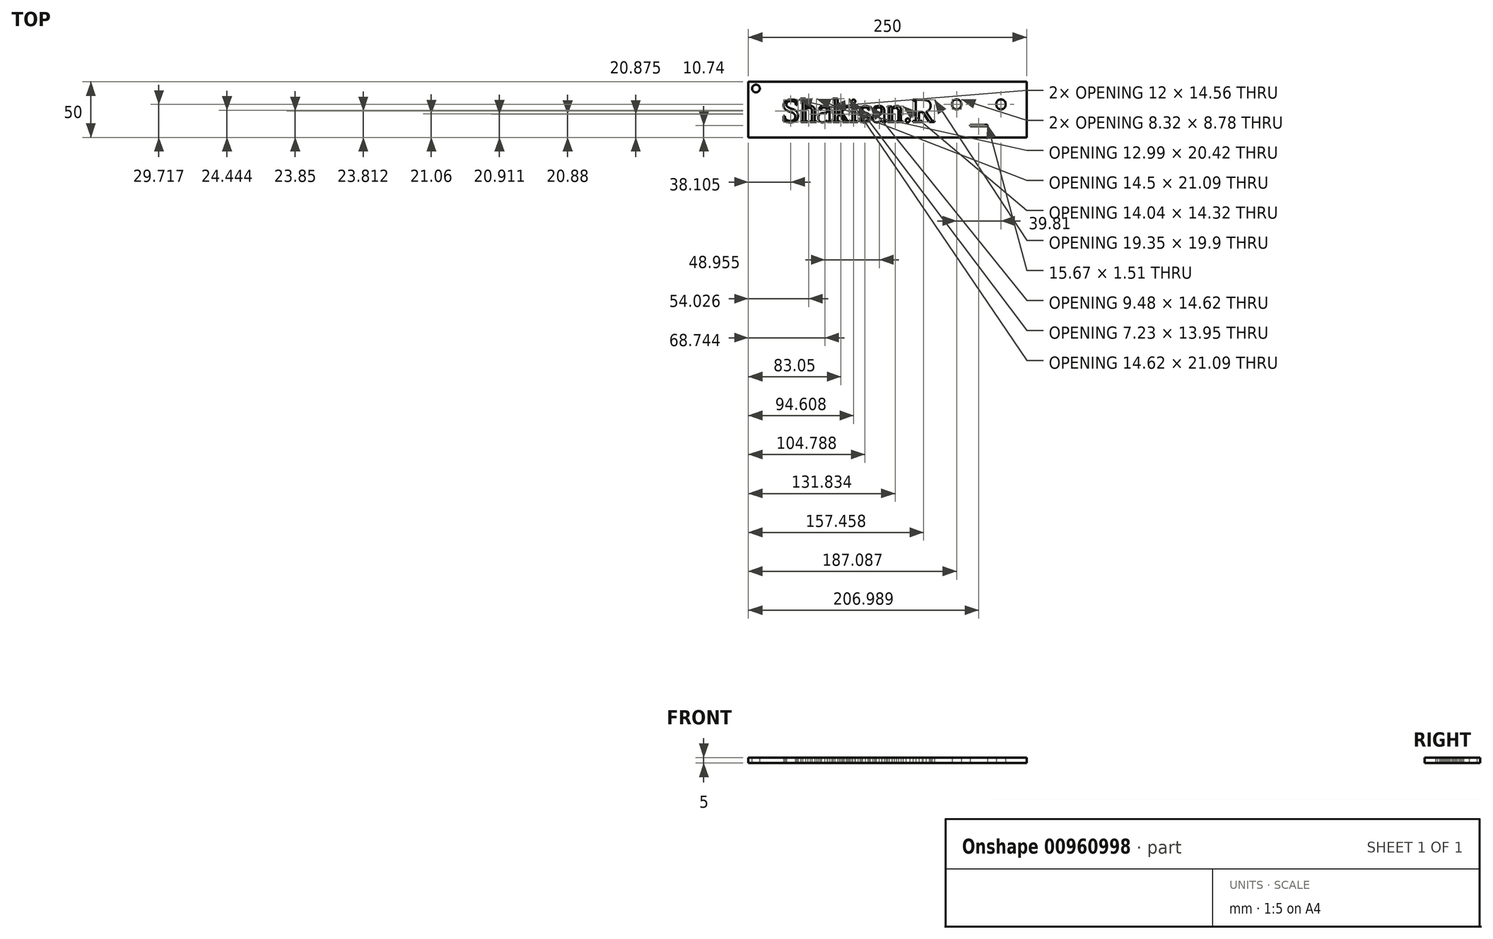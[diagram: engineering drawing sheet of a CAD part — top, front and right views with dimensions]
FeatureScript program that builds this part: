
annotation { "Feature Type Name" : "Feature", "Feature Type Description" : "" }
export const myFeature = defineFeature(function(context is Context, id is Id, definition is map)
    precondition{}
    {
        {
            var Q0;
            Q0=qCreatedBy(makeId("Top.planeOp"),FACE);
            var sketch = newSketch(context, id + "F0", { "sketchPlane" : qUnion([Q0])});
            skLineSegment(sketch, "E0.bottom", {"start": v(21.25, 46.83) * mm, "end": v(271.25, 46.83) * mm});
            skLineSegment(sketch, "E0.top", {"start": v(21.25, -3.17) * mm, "end": v(271.25, -3.17) * mm});
            skLineSegment(sketch, "E0.left", {"start": v(21.25, 46.83) * mm, "end": v(21.25, -3.17) * mm});
            skLineSegment(sketch, "E0.right", {"start": v(271.25, 46.83) * mm, "end": v(271.25, -3.17) * mm});
            skText(sketch, "E1", { "text": "Shakisan.R  º _ º ", "fontName": "Tinos-Regular.ttf"});
            const initialGuessF0  = {"E1": [0.05083, 0.01073, 1, 0, 0.02188]};
            skSetInitialGuess(sketch, initialGuessF0);
            skSolve(sketch);
        }
        {
            var Q0;
            Q0 = qSketchRegion(id + "F0", true);
            extrude(context, id + "F1", {"entities" : qUnion([Q0]), "depth" : 5 * mm, "offsetDistance" : 25 * mm});
        }
        {
            var Q0;
            Q0=makeQuery(id+"F1.opExtrude","CAP_FACE",FACE,{"disambiguationData":[OSD([sQuery(id+"F0.wireOp",EDGE,"E0.bottom"),sQuery(id+"F0.wireOp",EDGE,"E0.top"),sQuery(id+"F0.wireOp",EDGE,"E0.left"),sQuery(id+"F0.wireOp",EDGE,"E0.right"),sQuery(id+"F0.wireOp",EDGE,"52a1acff-9716-4e03-b524-4271869a984e.sketch_text.stroke-0"),sQuery(id+"F0.wireOp",EDGE,"52a1acff-9716-4e03-b524-4271869a984e.sketch_text.stroke-1"),sQuery(id+"F0.wireOp",EDGE,"52a1acff-9716-4e03-b524-4271869a984e.sketch_text.stroke-2"),sQuery(id+"F0.wireOp",EDGE,"52a1acff-9716-4e03-b524-4271869a984e.sketch_text.stroke-3"),sQuery(id+"F0.wireOp",EDGE,"52a1acff-9716-4e03-b524-4271869a984e.sketch_text.stroke-4"),sQuery(id+"F0.wireOp",EDGE,"52a1acff-9716-4e03-b524-4271869a984e.sketch_text.stroke-5"),sQuery(id+"F0.wireOp",EDGE,"52a1acff-9716-4e03-b524-4271869a984e.sketch_text.stroke-6"),sQuery(id+"F0.wireOp",EDGE,"52a1acff-9716-4e03-b524-4271869a984e.sketch_text.stroke-7"),sQuery(id+"F0.wireOp",EDGE,"52a1acff-9716-4e03-b524-4271869a984e.sketch_text.stroke-8"),sQuery(id+"F0.wireOp",EDGE,"52a1acff-9716-4e03-b524-4271869a984e.sketch_text.stroke-9"),sQuery(id+"F0.wireOp",EDGE,"52a1acff-9716-4e03-b524-4271869a984e.sketch_text.stroke-10"),sQuery(id+"F0.wireOp",EDGE,"52a1acff-9716-4e03-b524-4271869a984e.sketch_text.stroke-11"),sQuery(id+"F0.wireOp",EDGE,"52a1acff-9716-4e03-b524-4271869a984e.sketch_text.stroke-12"),sQuery(id+"F0.wireOp",EDGE,"52a1acff-9716-4e03-b524-4271869a984e.sketch_text.stroke-13"),sQuery(id+"F0.wireOp",EDGE,"52a1acff-9716-4e03-b524-4271869a984e.sketch_text.stroke-14"),sQuery(id+"F0.wireOp",EDGE,"52a1acff-9716-4e03-b524-4271869a984e.sketch_text.stroke-15"),sQuery(id+"F0.wireOp",EDGE,"52a1acff-9716-4e03-b524-4271869a984e.sketch_text.stroke-16"),sQuery(id+"F0.wireOp",EDGE,"52a1acff-9716-4e03-b524-4271869a984e.sketch_text.stroke-17"),sQuery(id+"F0.wireOp",EDGE,"52a1acff-9716-4e03-b524-4271869a984e.sketch_text.stroke-18"),sQuery(id+"F0.wireOp",EDGE,"52a1acff-9716-4e03-b524-4271869a984e.sketch_text.stroke-19"),sQuery(id+"F0.wireOp",EDGE,"52a1acff-9716-4e03-b524-4271869a984e.sketch_text.stroke-20"),sQuery(id+"F0.wireOp",EDGE,"52a1acff-9716-4e03-b524-4271869a984e.sketch_text.stroke-21"),sQuery(id+"F0.wireOp",EDGE,"52a1acff-9716-4e03-b524-4271869a984e.sketch_text.stroke-22"),sQuery(id+"F0.wireOp",EDGE,"52a1acff-9716-4e03-b524-4271869a984e.sketch_text.stroke-23"),sQuery(id+"F0.wireOp",EDGE,"52a1acff-9716-4e03-b524-4271869a984e.sketch_text.stroke-24"),sQuery(id+"F0.wireOp",EDGE,"52a1acff-9716-4e03-b524-4271869a984e.sketch_text.stroke-25"),sQuery(id+"F0.wireOp",EDGE,"52a1acff-9716-4e03-b524-4271869a984e.sketch_text.stroke-26"),sQuery(id+"F0.wireOp",EDGE,"52a1acff-9716-4e03-b524-4271869a984e.sketch_text.stroke-27"),sQuery(id+"F0.wireOp",EDGE,"52a1acff-9716-4e03-b524-4271869a984e.sketch_text.stroke-28"),sQuery(id+"F0.wireOp",EDGE,"52a1acff-9716-4e03-b524-4271869a984e.sketch_text.stroke-29"),sQuery(id+"F0.wireOp",EDGE,"52a1acff-9716-4e03-b524-4271869a984e.sketch_text.stroke-30"),sQuery(id+"F0.wireOp",EDGE,"52a1acff-9716-4e03-b524-4271869a984e.sketch_text.stroke-31"),sQuery(id+"F0.wireOp",EDGE,"52a1acff-9716-4e03-b524-4271869a984e.sketch_text.stroke-32"),sQuery(id+"F0.wireOp",EDGE,"52a1acff-9716-4e03-b524-4271869a984e.sketch_text.stroke-33"),sQuery(id+"F0.wireOp",EDGE,"52a1acff-9716-4e03-b524-4271869a984e.sketch_text.stroke-34"),sQuery(id+"F0.wireOp",EDGE,"52a1acff-9716-4e03-b524-4271869a984e.sketch_text.stroke-35"),sQuery(id+"F0.wireOp",EDGE,"52a1acff-9716-4e03-b524-4271869a984e.sketch_text.stroke-36"),sQuery(id+"F0.wireOp",EDGE,"52a1acff-9716-4e03-b524-4271869a984e.sketch_text.stroke-37"),sQuery(id+"F0.wireOp",EDGE,"52a1acff-9716-4e03-b524-4271869a984e.sketch_text.stroke-38"),sQuery(id+"F0.wireOp",EDGE,"52a1acff-9716-4e03-b524-4271869a984e.sketch_text.stroke-39"),sQuery(id+"F0.wireOp",EDGE,"52a1acff-9716-4e03-b524-4271869a984e.sketch_text.stroke-40"),sQuery(id+"F0.wireOp",EDGE,"52a1acff-9716-4e03-b524-4271869a984e.sketch_text.stroke-41"),sQuery(id+"F0.wireOp",EDGE,"52a1acff-9716-4e03-b524-4271869a984e.sketch_text.stroke-42"),sQuery(id+"F0.wireOp",EDGE,"52a1acff-9716-4e03-b524-4271869a984e.sketch_text.stroke-43"),sQuery(id+"F0.wireOp",EDGE,"52a1acff-9716-4e03-b524-4271869a984e.sketch_text.stroke-44"),sQuery(id+"F0.wireOp",EDGE,"52a1acff-9716-4e03-b524-4271869a984e.sketch_text.stroke-45"),sQuery(id+"F0.wireOp",EDGE,"52a1acff-9716-4e03-b524-4271869a984e.sketch_text.stroke-46"),sQuery(id+"F0.wireOp",EDGE,"52a1acff-9716-4e03-b524-4271869a984e.sketch_text.stroke-47"),sQuery(id+"F0.wireOp",EDGE,"52a1acff-9716-4e03-b524-4271869a984e.sketch_text.stroke-48"),sQuery(id+"F0.wireOp",EDGE,"52a1acff-9716-4e03-b524-4271869a984e.sketch_text.stroke-49"),sQuery(id+"F0.wireOp",EDGE,"52a1acff-9716-4e03-b524-4271869a984e.sketch_text.stroke-50"),sQuery(id+"F0.wireOp",EDGE,"52a1acff-9716-4e03-b524-4271869a984e.sketch_text.stroke-51"),sQuery(id+"F0.wireOp",EDGE,"52a1acff-9716-4e03-b524-4271869a984e.sketch_text.stroke-52"),sQuery(id+"F0.wireOp",EDGE,"52a1acff-9716-4e03-b524-4271869a984e.sketch_text.stroke-53"),sQuery(id+"F0.wireOp",EDGE,"52a1acff-9716-4e03-b524-4271869a984e.sketch_text.stroke-54"),sQuery(id+"F0.wireOp",EDGE,"52a1acff-9716-4e03-b524-4271869a984e.sketch_text.stroke-55"),sQuery(id+"F0.wireOp",EDGE,"52a1acff-9716-4e03-b524-4271869a984e.sketch_text.stroke-56"),sQuery(id+"F0.wireOp",EDGE,"52a1acff-9716-4e03-b524-4271869a984e.sketch_text.stroke-57"),sQuery(id+"F0.wireOp",EDGE,"52a1acff-9716-4e03-b524-4271869a984e.sketch_text.stroke-58"),sQuery(id+"F0.wireOp",EDGE,"52a1acff-9716-4e03-b524-4271869a984e.sketch_text.stroke-59"),sQuery(id+"F0.wireOp",EDGE,"52a1acff-9716-4e03-b524-4271869a984e.sketch_text.stroke-60"),sQuery(id+"F0.wireOp",EDGE,"52a1acff-9716-4e03-b524-4271869a984e.sketch_text.stroke-61"),sQuery(id+"F0.wireOp",EDGE,"52a1acff-9716-4e03-b524-4271869a984e.sketch_text.stroke-62"),sQuery(id+"F0.wireOp",EDGE,"52a1acff-9716-4e03-b524-4271869a984e.sketch_text.stroke-63"),sQuery(id+"F0.wireOp",EDGE,"52a1acff-9716-4e03-b524-4271869a984e.sketch_text.stroke-64"),sQuery(id+"F0.wireOp",EDGE,"52a1acff-9716-4e03-b524-4271869a984e.sketch_text.stroke-65"),sQuery(id+"F0.wireOp",EDGE,"52a1acff-9716-4e03-b524-4271869a984e.sketch_text.stroke-66"),sQuery(id+"F0.wireOp",EDGE,"52a1acff-9716-4e03-b524-4271869a984e.sketch_text.stroke-67"),sQuery(id+"F0.wireOp",EDGE,"52a1acff-9716-4e03-b524-4271869a984e.sketch_text.stroke-68"),sQuery(id+"F0.wireOp",EDGE,"52a1acff-9716-4e03-b524-4271869a984e.sketch_text.stroke-69"),sQuery(id+"F0.wireOp",EDGE,"52a1acff-9716-4e03-b524-4271869a984e.sketch_text.stroke-70"),sQuery(id+"F0.wireOp",EDGE,"52a1acff-9716-4e03-b524-4271869a984e.sketch_text.stroke-71"),sQuery(id+"F0.wireOp",EDGE,"52a1acff-9716-4e03-b524-4271869a984e.sketch_text.stroke-72"),sQuery(id+"F0.wireOp",EDGE,"52a1acff-9716-4e03-b524-4271869a984e.sketch_text.stroke-73"),sQuery(id+"F0.wireOp",EDGE,"52a1acff-9716-4e03-b524-4271869a984e.sketch_text.stroke-74"),sQuery(id+"F0.wireOp",EDGE,"52a1acff-9716-4e03-b524-4271869a984e.sketch_text.stroke-75"),sQuery(id+"F0.wireOp",EDGE,"52a1acff-9716-4e03-b524-4271869a984e.sketch_text.stroke-76"),sQuery(id+"F0.wireOp",EDGE,"52a1acff-9716-4e03-b524-4271869a984e.sketch_text.stroke-77"),sQuery(id+"F0.wireOp",EDGE,"52a1acff-9716-4e03-b524-4271869a984e.sketch_text.stroke-78"),sQuery(id+"F0.wireOp",EDGE,"52a1acff-9716-4e03-b524-4271869a984e.sketch_text.stroke-79"),sQuery(id+"F0.wireOp",EDGE,"52a1acff-9716-4e03-b524-4271869a984e.sketch_text.stroke-80"),sQuery(id+"F0.wireOp",EDGE,"52a1acff-9716-4e03-b524-4271869a984e.sketch_text.stroke-81"),sQuery(id+"F0.wireOp",EDGE,"52a1acff-9716-4e03-b524-4271869a984e.sketch_text.stroke-89"),sQuery(id+"F0.wireOp",EDGE,"52a1acff-9716-4e03-b524-4271869a984e.sketch_text.stroke-90"),sQuery(id+"F0.wireOp",EDGE,"52a1acff-9716-4e03-b524-4271869a984e.sketch_text.stroke-91"),sQuery(id+"F0.wireOp",EDGE,"52a1acff-9716-4e03-b524-4271869a984e.sketch_text.stroke-92"),sQuery(id+"F0.wireOp",EDGE,"52a1acff-9716-4e03-b524-4271869a984e.sketch_text.stroke-93"),sQuery(id+"F0.wireOp",EDGE,"52a1acff-9716-4e03-b524-4271869a984e.sketch_text.stroke-94"),sQuery(id+"F0.wireOp",EDGE,"52a1acff-9716-4e03-b524-4271869a984e.sketch_text.stroke-95"),sQuery(id+"F0.wireOp",EDGE,"52a1acff-9716-4e03-b524-4271869a984e.sketch_text.stroke-96"),sQuery(id+"F0.wireOp",EDGE,"52a1acff-9716-4e03-b524-4271869a984e.sketch_text.stroke-97"),sQuery(id+"F0.wireOp",EDGE,"52a1acff-9716-4e03-b524-4271869a984e.sketch_text.stroke-98"),sQuery(id+"F0.wireOp",EDGE,"52a1acff-9716-4e03-b524-4271869a984e.sketch_text.stroke-99"),sQuery(id+"F0.wireOp",EDGE,"52a1acff-9716-4e03-b524-4271869a984e.sketch_text.stroke-100"),sQuery(id+"F0.wireOp",EDGE,"52a1acff-9716-4e03-b524-4271869a984e.sketch_text.stroke-101"),sQuery(id+"F0.wireOp",EDGE,"52a1acff-9716-4e03-b524-4271869a984e.sketch_text.stroke-102"),sQuery(id+"F0.wireOp",EDGE,"52a1acff-9716-4e03-b524-4271869a984e.sketch_text.stroke-103"),sQuery(id+"F0.wireOp",EDGE,"52a1acff-9716-4e03-b524-4271869a984e.sketch_text.stroke-104"),sQuery(id+"F0.wireOp",EDGE,"52a1acff-9716-4e03-b524-4271869a984e.sketch_text.stroke-105"),sQuery(id+"F0.wireOp",EDGE,"52a1acff-9716-4e03-b524-4271869a984e.sketch_text.stroke-106"),sQuery(id+"F0.wireOp",EDGE,"52a1acff-9716-4e03-b524-4271869a984e.sketch_text.stroke-107"),sQuery(id+"F0.wireOp",EDGE,"52a1acff-9716-4e03-b524-4271869a984e.sketch_text.stroke-108"),sQuery(id+"F0.wireOp",EDGE,"52a1acff-9716-4e03-b524-4271869a984e.sketch_text.stroke-109"),sQuery(id+"F0.wireOp",EDGE,"52a1acff-9716-4e03-b524-4271869a984e.sketch_text.stroke-110"),sQuery(id+"F0.wireOp",EDGE,"52a1acff-9716-4e03-b524-4271869a984e.sketch_text.stroke-111"),sQuery(id+"F0.wireOp",EDGE,"52a1acff-9716-4e03-b524-4271869a984e.sketch_text.stroke-112"),sQuery(id+"F0.wireOp",EDGE,"52a1acff-9716-4e03-b524-4271869a984e.sketch_text.stroke-113"),sQuery(id+"F0.wireOp",EDGE,"52a1acff-9716-4e03-b524-4271869a984e.sketch_text.stroke-114"),sQuery(id+"F0.wireOp",EDGE,"52a1acff-9716-4e03-b524-4271869a984e.sketch_text.stroke-115"),sQuery(id+"F0.wireOp",EDGE,"52a1acff-9716-4e03-b524-4271869a984e.sketch_text.stroke-116"),sQuery(id+"F0.wireOp",EDGE,"52a1acff-9716-4e03-b524-4271869a984e.sketch_text.stroke-117"),sQuery(id+"F0.wireOp",EDGE,"52a1acff-9716-4e03-b524-4271869a984e.sketch_text.stroke-118"),sQuery(id+"F0.wireOp",EDGE,"52a1acff-9716-4e03-b524-4271869a984e.sketch_text.stroke-119"),sQuery(id+"F0.wireOp",EDGE,"52a1acff-9716-4e03-b524-4271869a984e.sketch_text.stroke-120"),sQuery(id+"F0.wireOp",EDGE,"52a1acff-9716-4e03-b524-4271869a984e.sketch_text.stroke-121"),sQuery(id+"F0.wireOp",EDGE,"52a1acff-9716-4e03-b524-4271869a984e.sketch_text.stroke-122"),sQuery(id+"F0.wireOp",EDGE,"52a1acff-9716-4e03-b524-4271869a984e.sketch_text.stroke-123"),sQuery(id+"F0.wireOp",EDGE,"52a1acff-9716-4e03-b524-4271869a984e.sketch_text.stroke-124"),sQuery(id+"F0.wireOp",EDGE,"52a1acff-9716-4e03-b524-4271869a984e.sketch_text.stroke-125"),sQuery(id+"F0.wireOp",EDGE,"52a1acff-9716-4e03-b524-4271869a984e.sketch_text.stroke-126"),sQuery(id+"F0.wireOp",EDGE,"52a1acff-9716-4e03-b524-4271869a984e.sketch_text.stroke-127"),sQuery(id+"F0.wireOp",EDGE,"52a1acff-9716-4e03-b524-4271869a984e.sketch_text.stroke-128"),sQuery(id+"F0.wireOp",EDGE,"52a1acff-9716-4e03-b524-4271869a984e.sketch_text.stroke-129"),sQuery(id+"F0.wireOp",EDGE,"52a1acff-9716-4e03-b524-4271869a984e.sketch_text.stroke-130"),sQuery(id+"F0.wireOp",EDGE,"52a1acff-9716-4e03-b524-4271869a984e.sketch_text.stroke-131"),sQuery(id+"F0.wireOp",EDGE,"52a1acff-9716-4e03-b524-4271869a984e.sketch_text.stroke-132"),sQuery(id+"F0.wireOp",EDGE,"52a1acff-9716-4e03-b524-4271869a984e.sketch_text.stroke-133"),sQuery(id+"F0.wireOp",EDGE,"52a1acff-9716-4e03-b524-4271869a984e.sketch_text.stroke-134"),sQuery(id+"F0.wireOp",EDGE,"52a1acff-9716-4e03-b524-4271869a984e.sketch_text.stroke-135"),sQuery(id+"F0.wireOp",EDGE,"52a1acff-9716-4e03-b524-4271869a984e.sketch_text.stroke-136"),sQuery(id+"F0.wireOp",EDGE,"52a1acff-9716-4e03-b524-4271869a984e.sketch_text.stroke-137"),sQuery(id+"F0.wireOp",EDGE,"52a1acff-9716-4e03-b524-4271869a984e.sketch_text.stroke-138"),sQuery(id+"F0.wireOp",EDGE,"52a1acff-9716-4e03-b524-4271869a984e.sketch_text.stroke-139"),sQuery(id+"F0.wireOp",EDGE,"52a1acff-9716-4e03-b524-4271869a984e.sketch_text.stroke-140"),sQuery(id+"F0.wireOp",EDGE,"52a1acff-9716-4e03-b524-4271869a984e.sketch_text.stroke-141"),sQuery(id+"F0.wireOp",EDGE,"52a1acff-9716-4e03-b524-4271869a984e.sketch_text.stroke-142"),sQuery(id+"F0.wireOp",EDGE,"52a1acff-9716-4e03-b524-4271869a984e.sketch_text.stroke-143"),sQuery(id+"F0.wireOp",EDGE,"52a1acff-9716-4e03-b524-4271869a984e.sketch_text.stroke-144"),sQuery(id+"F0.wireOp",EDGE,"52a1acff-9716-4e03-b524-4271869a984e.sketch_text.stroke-145"),sQuery(id+"F0.wireOp",EDGE,"52a1acff-9716-4e03-b524-4271869a984e.sketch_text.stroke-146"),sQuery(id+"F0.wireOp",EDGE,"52a1acff-9716-4e03-b524-4271869a984e.sketch_text.stroke-147"),sQuery(id+"F0.wireOp",EDGE,"52a1acff-9716-4e03-b524-4271869a984e.sketch_text.stroke-148"),sQuery(id+"F0.wireOp",EDGE,"52a1acff-9716-4e03-b524-4271869a984e.sketch_text.stroke-149"),sQuery(id+"F0.wireOp",EDGE,"52a1acff-9716-4e03-b524-4271869a984e.sketch_text.stroke-150"),sQuery(id+"F0.wireOp",EDGE,"52a1acff-9716-4e03-b524-4271869a984e.sketch_text.stroke-151"),sQuery(id+"F0.wireOp",EDGE,"52a1acff-9716-4e03-b524-4271869a984e.sketch_text.stroke-152"),sQuery(id+"F0.wireOp",EDGE,"52a1acff-9716-4e03-b524-4271869a984e.sketch_text.stroke-153"),sQuery(id+"F0.wireOp",EDGE,"52a1acff-9716-4e03-b524-4271869a984e.sketch_text.stroke-154"),sQuery(id+"F0.wireOp",EDGE,"52a1acff-9716-4e03-b524-4271869a984e.sketch_text.stroke-155"),sQuery(id+"F0.wireOp",EDGE,"52a1acff-9716-4e03-b524-4271869a984e.sketch_text.stroke-156"),sQuery(id+"F0.wireOp",EDGE,"52a1acff-9716-4e03-b524-4271869a984e.sketch_text.stroke-157"),sQuery(id+"F0.wireOp",EDGE,"52a1acff-9716-4e03-b524-4271869a984e.sketch_text.stroke-158"),sQuery(id+"F0.wireOp",EDGE,"52a1acff-9716-4e03-b524-4271869a984e.sketch_text.stroke-159"),sQuery(id+"F0.wireOp",EDGE,"52a1acff-9716-4e03-b524-4271869a984e.sketch_text.stroke-160"),sQuery(id+"F0.wireOp",EDGE,"52a1acff-9716-4e03-b524-4271869a984e.sketch_text.stroke-161"),sQuery(id+"F0.wireOp",EDGE,"52a1acff-9716-4e03-b524-4271869a984e.sketch_text.stroke-162"),sQuery(id+"F0.wireOp",EDGE,"52a1acff-9716-4e03-b524-4271869a984e.sketch_text.stroke-163"),sQuery(id+"F0.wireOp",EDGE,"52a1acff-9716-4e03-b524-4271869a984e.sketch_text.stroke-164"),sQuery(id+"F0.wireOp",EDGE,"52a1acff-9716-4e03-b524-4271869a984e.sketch_text.stroke-165"),sQuery(id+"F0.wireOp",EDGE,"52a1acff-9716-4e03-b524-4271869a984e.sketch_text.stroke-166"),sQuery(id+"F0.wireOp",EDGE,"52a1acff-9716-4e03-b524-4271869a984e.sketch_text.stroke-167"),sQuery(id+"F0.wireOp",EDGE,"52a1acff-9716-4e03-b524-4271869a984e.sketch_text.stroke-168"),sQuery(id+"F0.wireOp",EDGE,"52a1acff-9716-4e03-b524-4271869a984e.sketch_text.stroke-169"),sQuery(id+"F0.wireOp",EDGE,"52a1acff-9716-4e03-b524-4271869a984e.sketch_text.stroke-170"),sQuery(id+"F0.wireOp",EDGE,"52a1acff-9716-4e03-b524-4271869a984e.sketch_text.stroke-171"),sQuery(id+"F0.wireOp",EDGE,"52a1acff-9716-4e03-b524-4271869a984e.sketch_text.stroke-172"),sQuery(id+"F0.wireOp",EDGE,"52a1acff-9716-4e03-b524-4271869a984e.sketch_text.stroke-173"),sQuery(id+"F0.wireOp",EDGE,"52a1acff-9716-4e03-b524-4271869a984e.sketch_text.stroke-174"),sQuery(id+"F0.wireOp",EDGE,"52a1acff-9716-4e03-b524-4271869a984e.sketch_text.stroke-175"),sQuery(id+"F0.wireOp",EDGE,"52a1acff-9716-4e03-b524-4271869a984e.sketch_text.stroke-176"),sQuery(id+"F0.wireOp",EDGE,"52a1acff-9716-4e03-b524-4271869a984e.sketch_text.stroke-177"),sQuery(id+"F0.wireOp",EDGE,"52a1acff-9716-4e03-b524-4271869a984e.sketch_text.stroke-178"),sQuery(id+"F0.wireOp",EDGE,"52a1acff-9716-4e03-b524-4271869a984e.sketch_text.stroke-179"),sQuery(id+"F0.wireOp",EDGE,"52a1acff-9716-4e03-b524-4271869a984e.sketch_text.stroke-180"),sQuery(id+"F0.wireOp",EDGE,"52a1acff-9716-4e03-b524-4271869a984e.sketch_text.stroke-181"),sQuery(id+"F0.wireOp",EDGE,"52a1acff-9716-4e03-b524-4271869a984e.sketch_text.stroke-182"),sQuery(id+"F0.wireOp",EDGE,"52a1acff-9716-4e03-b524-4271869a984e.sketch_text.stroke-190"),sQuery(id+"F0.wireOp",EDGE,"52a1acff-9716-4e03-b524-4271869a984e.sketch_text.stroke-191"),sQuery(id+"F0.wireOp",EDGE,"52a1acff-9716-4e03-b524-4271869a984e.sketch_text.stroke-192"),sQuery(id+"F0.wireOp",EDGE,"52a1acff-9716-4e03-b524-4271869a984e.sketch_text.stroke-193"),sQuery(id+"F0.wireOp",EDGE,"52a1acff-9716-4e03-b524-4271869a984e.sketch_text.stroke-194"),sQuery(id+"F0.wireOp",EDGE,"52a1acff-9716-4e03-b524-4271869a984e.sketch_text.stroke-195"),sQuery(id+"F0.wireOp",EDGE,"52a1acff-9716-4e03-b524-4271869a984e.sketch_text.stroke-196"),sQuery(id+"F0.wireOp",EDGE,"52a1acff-9716-4e03-b524-4271869a984e.sketch_text.stroke-197"),sQuery(id+"F0.wireOp",EDGE,"52a1acff-9716-4e03-b524-4271869a984e.sketch_text.stroke-198"),sQuery(id+"F0.wireOp",EDGE,"52a1acff-9716-4e03-b524-4271869a984e.sketch_text.stroke-199"),sQuery(id+"F0.wireOp",EDGE,"52a1acff-9716-4e03-b524-4271869a984e.sketch_text.stroke-200"),sQuery(id+"F0.wireOp",EDGE,"52a1acff-9716-4e03-b524-4271869a984e.sketch_text.stroke-201"),sQuery(id+"F0.wireOp",EDGE,"52a1acff-9716-4e03-b524-4271869a984e.sketch_text.stroke-202"),sQuery(id+"F0.wireOp",EDGE,"52a1acff-9716-4e03-b524-4271869a984e.sketch_text.stroke-203"),sQuery(id+"F0.wireOp",EDGE,"52a1acff-9716-4e03-b524-4271869a984e.sketch_text.stroke-204"),sQuery(id+"F0.wireOp",EDGE,"52a1acff-9716-4e03-b524-4271869a984e.sketch_text.stroke-205"),sQuery(id+"F0.wireOp",EDGE,"52a1acff-9716-4e03-b524-4271869a984e.sketch_text.stroke-206"),sQuery(id+"F0.wireOp",EDGE,"52a1acff-9716-4e03-b524-4271869a984e.sketch_text.stroke-207"),sQuery(id+"F0.wireOp",EDGE,"52a1acff-9716-4e03-b524-4271869a984e.sketch_text.stroke-208"),sQuery(id+"F0.wireOp",EDGE,"52a1acff-9716-4e03-b524-4271869a984e.sketch_text.stroke-209"),sQuery(id+"F0.wireOp",EDGE,"52a1acff-9716-4e03-b524-4271869a984e.sketch_text.stroke-210"),sQuery(id+"F0.wireOp",EDGE,"52a1acff-9716-4e03-b524-4271869a984e.sketch_text.stroke-211"),sQuery(id+"F0.wireOp",EDGE,"52a1acff-9716-4e03-b524-4271869a984e.sketch_text.stroke-212"),sQuery(id+"F0.wireOp",EDGE,"52a1acff-9716-4e03-b524-4271869a984e.sketch_text.stroke-213"),sQuery(id+"F0.wireOp",EDGE,"52a1acff-9716-4e03-b524-4271869a984e.sketch_text.stroke-214"),sQuery(id+"F0.wireOp",EDGE,"52a1acff-9716-4e03-b524-4271869a984e.sketch_text.stroke-215"),sQuery(id+"F0.wireOp",EDGE,"52a1acff-9716-4e03-b524-4271869a984e.sketch_text.stroke-216"),sQuery(id+"F0.wireOp",EDGE,"52a1acff-9716-4e03-b524-4271869a984e.sketch_text.stroke-217"),sQuery(id+"F0.wireOp",EDGE,"52a1acff-9716-4e03-b524-4271869a984e.sketch_text.stroke-218"),sQuery(id+"F0.wireOp",EDGE,"52a1acff-9716-4e03-b524-4271869a984e.sketch_text.stroke-219"),sQuery(id+"F0.wireOp",EDGE,"52a1acff-9716-4e03-b524-4271869a984e.sketch_text.stroke-220"),sQuery(id+"F0.wireOp",EDGE,"52a1acff-9716-4e03-b524-4271869a984e.sketch_text.stroke-221"),sQuery(id+"F0.wireOp",EDGE,"52a1acff-9716-4e03-b524-4271869a984e.sketch_text.stroke-222"),sQuery(id+"F0.wireOp",EDGE,"52a1acff-9716-4e03-b524-4271869a984e.sketch_text.stroke-223"),sQuery(id+"F0.wireOp",EDGE,"52a1acff-9716-4e03-b524-4271869a984e.sketch_text.stroke-224"),sQuery(id+"F0.wireOp",EDGE,"52a1acff-9716-4e03-b524-4271869a984e.sketch_text.stroke-225"),sQuery(id+"F0.wireOp",EDGE,"52a1acff-9716-4e03-b524-4271869a984e.sketch_text.stroke-226"),sQuery(id+"F0.wireOp",EDGE,"52a1acff-9716-4e03-b524-4271869a984e.sketch_text.stroke-227"),sQuery(id+"F0.wireOp",EDGE,"52a1acff-9716-4e03-b524-4271869a984e.sketch_text.stroke-228"),sQuery(id+"F0.wireOp",EDGE,"52a1acff-9716-4e03-b524-4271869a984e.sketch_text.stroke-229"),sQuery(id+"F0.wireOp",EDGE,"52a1acff-9716-4e03-b524-4271869a984e.sketch_text.stroke-230"),sQuery(id+"F0.wireOp",EDGE,"52a1acff-9716-4e03-b524-4271869a984e.sketch_text.stroke-231"),sQuery(id+"F0.wireOp",EDGE,"52a1acff-9716-4e03-b524-4271869a984e.sketch_text.stroke-232"),sQuery(id+"F0.wireOp",EDGE,"52a1acff-9716-4e03-b524-4271869a984e.sketch_text.stroke-233"),sQuery(id+"F0.wireOp",EDGE,"52a1acff-9716-4e03-b524-4271869a984e.sketch_text.stroke-234"),sQuery(id+"F0.wireOp",EDGE,"52a1acff-9716-4e03-b524-4271869a984e.sketch_text.stroke-235"),sQuery(id+"F0.wireOp",EDGE,"52a1acff-9716-4e03-b524-4271869a984e.sketch_text.stroke-236"),sQuery(id+"F0.wireOp",EDGE,"52a1acff-9716-4e03-b524-4271869a984e.sketch_text.stroke-237"),sQuery(id+"F0.wireOp",EDGE,"52a1acff-9716-4e03-b524-4271869a984e.sketch_text.stroke-238"),sQuery(id+"F0.wireOp",EDGE,"52a1acff-9716-4e03-b524-4271869a984e.sketch_text.stroke-239"),sQuery(id+"F0.wireOp",EDGE,"52a1acff-9716-4e03-b524-4271869a984e.sketch_text.stroke-240"),sQuery(id+"F0.wireOp",EDGE,"52a1acff-9716-4e03-b524-4271869a984e.sketch_text.stroke-241"),sQuery(id+"F0.wireOp",EDGE,"52a1acff-9716-4e03-b524-4271869a984e.sketch_text.stroke-242"),sQuery(id+"F0.wireOp",EDGE,"52a1acff-9716-4e03-b524-4271869a984e.sketch_text.stroke-250"),sQuery(id+"F0.wireOp",EDGE,"52a1acff-9716-4e03-b524-4271869a984e.sketch_text.stroke-251"),sQuery(id+"F0.wireOp",EDGE,"52a1acff-9716-4e03-b524-4271869a984e.sketch_text.stroke-252"),sQuery(id+"F0.wireOp",EDGE,"52a1acff-9716-4e03-b524-4271869a984e.sketch_text.stroke-253")])],"isStart":false});
            var sketch = newSketch(context, id + "F2", { "sketchPlane" : qUnion([Q0])});
            skCircle(sketch, "E2", {"center": v(28, 40.76) * mm, "radius": 3.5 * mm});
            skSolve(sketch);
        }
        {
            var Q0;
            Q0 = qSketchRegion(id + "F2", true);
            extrude(context, id + "F3", {"entities" : qUnion([Q0]), "operationType" : NewBodyOperationType.REMOVE, "oppositeDirection" : true, "depth" : 25 * mm, "offsetDistance" : 25 * mm});
        }
    });
